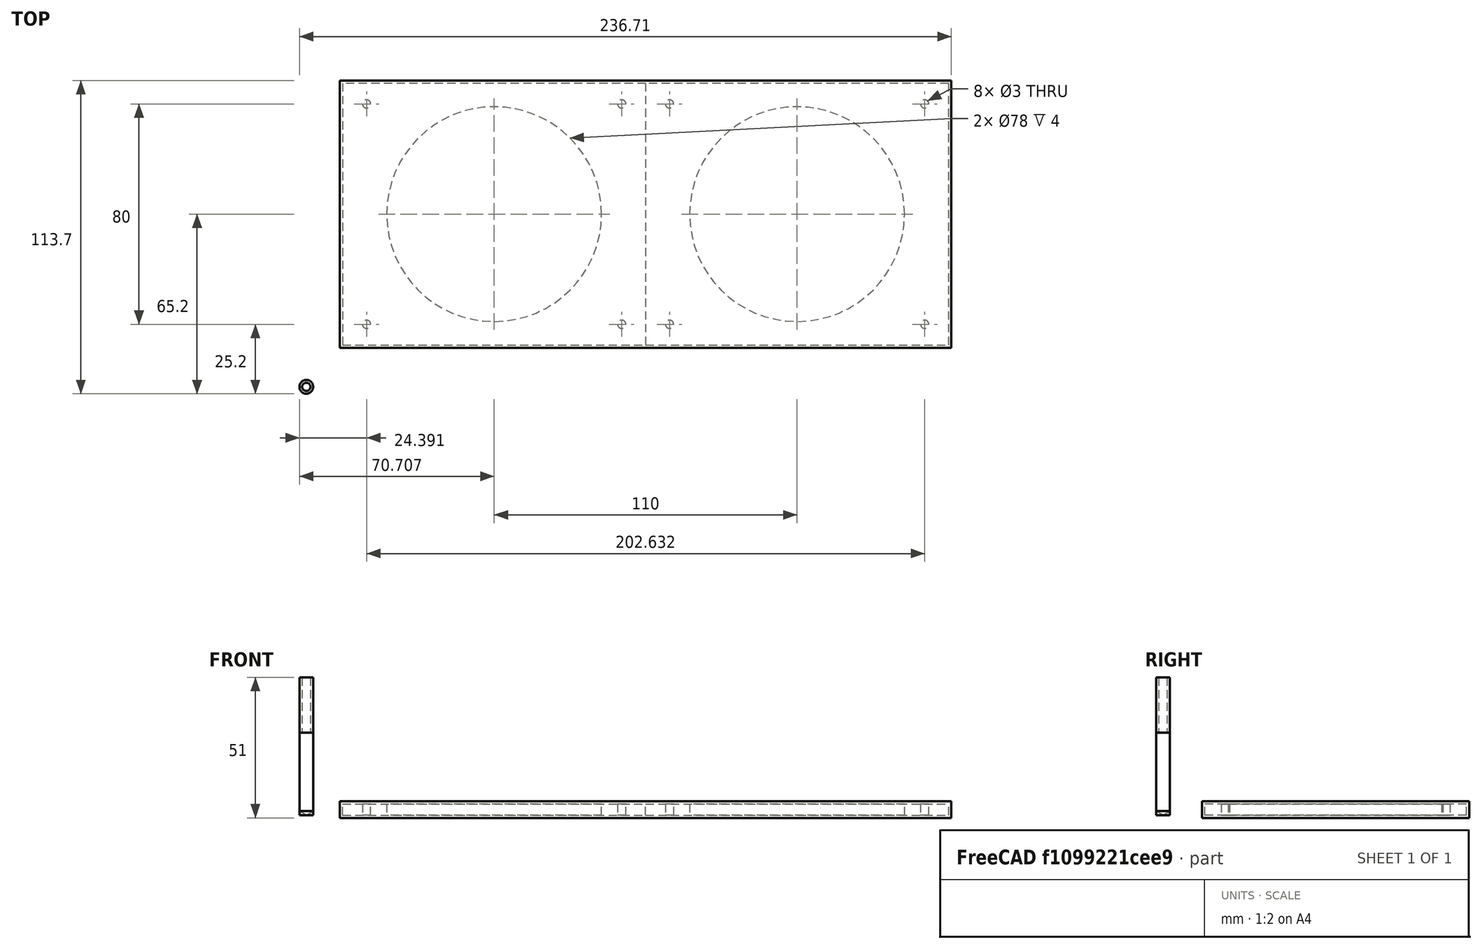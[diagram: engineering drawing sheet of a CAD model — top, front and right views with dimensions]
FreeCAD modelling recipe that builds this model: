
FCSTD DOCUMENT  (FreeCAD 1.0R39319 (Git))
Label: CAR_LASER_COMPONENTS_A4
License: All rights reserved
LicenseURL: https://en.wikipedia.org/wiki/All_rights_reserved
objects: Part::FeaturePython×10, App::FeaturePython×7, Path::FeaturePython×5, Sketcher::SketchObject×3, App::DocumentObjectGroup×3, PartDesign::Revolution×2, PartDesign::Body×2, Mesh::FeaturePython×1
note: 24 computed .brp shape members not serialized (recipe doc carries the construction recipe); baked Part::Feature solids carry a one-line shape summary decoded from their .brp

FEATURE [Sketcher::SketchObject] Sketch  label="A4"
  ArcFitTolerance = 0
  FullyConstrained = true
  MakeInternals = false
  sketch-geometry (12):
    g0: LineSegment [constr] StartX=0 StartY=0 StartZ=0 EndX=297 EndY=0 EndZ=0
    g1: LineSegment [constr] StartX=297 StartY=0 StartZ=0 EndX=297 EndY=420 EndZ=0
    g2: LineSegment [constr] StartX=297 StartY=420 StartZ=0 EndX=0 EndY=420 EndZ=0
    g3: LineSegment [constr] StartX=0 StartY=420 StartZ=0 EndX=0 EndY=0 EndZ=0
    g4: LineSegment StartX=0 StartY=0 StartZ=0 EndX=297 EndY=0 EndZ=0
    g5: LineSegment StartX=297 StartY=0 StartZ=0 EndX=297 EndY=420 EndZ=0
    g6: LineSegment StartX=297 StartY=420 StartZ=0 EndX=0 EndY=420 EndZ=0
    g7: LineSegment StartX=0 StartY=420 StartZ=0 EndX=0 EndY=0 EndZ=0
    g8: LineSegment [constr] StartX=0 StartY=420 StartZ=0 EndX=148.5 EndY=210 EndZ=0
    g9: LineSegment [constr] StartX=148.5 StartY=210 StartZ=0 EndX=297 EndY=0 EndZ=0
    g10: LineSegment StartX=148.5 StartY=210 StartZ=0 EndX=0 EndY=210 EndZ=0
    g11: LineSegment StartX=148.5 StartY=210 StartZ=0 EndX=297 EndY=210 EndZ=0
  constraints (30):
    c: Coincident(g0,g1)
    c: Coincident(g1,g2)
    c: Coincident(g2,g3)
    c: Coincident(g3,g0)
    c: Horizontal(g0)
    c: Horizontal(g2)
    c: Vertical(g1)
    c: Vertical(g3)
    c: Coincident(g0,g-1)
    c: DistanceY(g1,g1) = 420
    c: DistanceX(g2,g2) = 297
    c: Coincident(g4,g5)
    c: Coincident(g5,g6)
    c: Coincident(g6,g7)
    c: Coincident(g7,g4)
    c: Horizontal(g4)
    c: Horizontal(g6)
    c: Vertical(g5)
    c: Vertical(g7)
    c: Coincident(g4,g0)
    c: Coincident(g5,g1)
    c: Coincident(g8,g2)
    c: Coincident(g9,g0)
    c: Coincident(g9,g8)
    c: Equal(g9,g8)
    c: Coincident(g10,g8)
    c: Symmetric(g7,g7,g10)
    c: Horizontal(g10)
    c: Coincident(g11,g8)
    c: Symmetric(g5,g5,g11)
FEATURE [Part::FeaturePython] b_stearing_Flange_001_  label="stearing_Flange_001"  # a2plus imported part (geometry in sourceFile) (typed FeaturePython)
  Placement = pos=(-103.9,-12.3,0) rot=(0,0,1;0rad)
  a2p_Version = 0.4.68
  fixedPosition = true
  objectType = a2pPart
  sourceFile = ./stearing_Flange.FCStd
  subassemblyImport = false
  timeLastImport = 1.77512e+09
  updateColors = true
FEATURE [Part::FeaturePython] b_stearing_Flange_001_001  label="stearing_Flange_002"  # a2plus imported part (geometry in sourceFile) (typed FeaturePython)
  Placement = pos=(6.10001,-12.3,0) rot=(0,0,1;0rad)
  a2p_Version = 0.4.68
  fixedPosition = false
  objectType = a2pPart
  sourceFile = ./stearing_Flange.FCStd
  subassemblyImport = false
  timeLastImport = 1.77512e+09
  updateColors = true
FEATURE [App::FeaturePython] planeCoincident_001  label="planeCoincident_001__stearing_Flange_002"  # a2plus constraint (typed FeaturePython)
  Object1 = b_stearing_Flange_001_
  Object2 = b_stearing_Flange_001_001
  ParentTreeObject = -> b_stearing_Flange_001_
  SubElement1 = Face2
  SubElement2 = Face2
  Suppressed = false
  Type = plane
  directionConstraint = 0
  offset = 0
FEATURE [App::FeaturePython] planeCoincident_001_mirror  label="planeCoincident_001__stearing_Flange_001"  # a2plus constraint (typed FeaturePython)
  Object1 = b_stearing_Flange_001_
  Object2 = b_stearing_Flange_001_001
  ParentTreeObject = -> b_stearing_Flange_001_001
  SubElement1 = Face2
  SubElement2 = Face2
  Suppressed = false
  Type = plane
  directionConstraint = 0
  offset = 0
FEATURE [App::FeaturePython] planeCoincident_002  label="planeCoincident_002__stearing_Flange_002"  # a2plus constraint (typed FeaturePython)
  Object1 = b_stearing_Flange_001_
  Object2 = b_stearing_Flange_001_001
  ParentTreeObject = -> b_stearing_Flange_001_
  SubElement1 = Face3
  SubElement2 = Face1
  Suppressed = false
  Type = plane
  directionConstraint = 1
  offset = 0
FEATURE [App::FeaturePython] planeCoincident_002_mirror  label="planeCoincident_002__stearing_Flange_001"  # a2plus constraint (typed FeaturePython)
  Object1 = b_stearing_Flange_001_
  Object2 = b_stearing_Flange_001_001
  ParentTreeObject = -> b_stearing_Flange_001_001
  SubElement1 = Face3
  SubElement2 = Face1
  Suppressed = false
  Type = plane
  directionConstraint = 1
  offset = 0
FEATURE [App::FeaturePython] SetupSheet  # Path/CAM operation (typed FeaturePython)
  ClearanceHeightExpression = OpStockZMax+SetupSheet.ClearanceHeightOffset
  ClearanceHeightOffset = 5
  CoolantMode = 0
  CoolantModes = None | Flood | Mist
  FinalDepthExpression = OpFinalDepth
  HorizRapid = 0
  SafeHeightExpression = OpStockZMax+SetupSheet.SafeHeightOffset
  SafeHeightOffset = 3
  StartDepthExpression = OpStartDepth
  StepDownExpression = OpToolDiameter
  VertRapid = 0
FEATURE [Part::FeaturePython] Clone  label="Model-stearing_Flange_001"  # Draft clone (typed FeaturePython)
  AttacherType = Attacher::AttachEngine3D
  Fuse = false
  Objects = -> [b_stearing_Flange_001_]
  PathResource = Model
  Placement = pos=(-103.9,-12.3,0) rot=(0,0,1;0rad)
  Scale = (1,1,1)
FEATURE [Part::FeaturePython] Clone001  label="Model-stearing_Flange_002"  # Draft clone (typed FeaturePython)
  AttacherType = Attacher::AttachEngine3D
  Fuse = false
  Objects = -> [b_stearing_Flange_001_001]
  PathResource = Model
  Placement = pos=(6.10001,-12.3,0) rot=(0,0,1;0rad)
  Scale = (1,1,1)
FEATURE [App::DocumentObjectGroup] Model
  Group = -> [Clone,Clone001]
FEATURE [Part::FeaturePython] ToolBit  label="Endmill"  # Path/CAM toolbit (typed FeaturePython)
  BitPropertyNames = Chipload | CuttingEdgeHeight | Diameter | Flutes | Length | Material | ShankDiameter | SpindleDirection
  BitShape = <path>
  Chipload = 0
  CuttingEdgeHeight = 30
  Diameter = 5
  Flutes = 0
  Length = 50
  Material = 0
  ShankDiameter = 3
  ShapeName = endmill
  SpindleDirection = 0
FEATURE [Part::FeaturePython] Stock  # WARN: FeaturePython — macro-defined, semantics opaque (R4)
  Base = -> Model
  ExtXneg = 1
  ExtXpos = 1
  ExtYneg = 1
  ExtYpos = 1
  ExtZneg = 1
  ExtZpos = 1
  Placement = pos=(13.2071,15.2,0) rot=(0,0,1;0rad)
  StockType = FromBase
FEATURE [Mesh::FeaturePython] CutMaterial  # WARN: FeaturePython — macro-defined, semantics opaque (R4)
FEATURE [Part::FeaturePython] ToolBit001  label="Endmill003"  # Path/CAM toolbit (typed FeaturePython)
  BitPropertyNames = Chipload | CuttingEdgeHeight | Diameter | Flutes | Length | Material | ShankDiameter | SpindleDirection
  BitShape = <path>
  Chipload = 0
  CuttingEdgeHeight = 30
  Diameter = 5
  Flutes = 0
  Length = 50
  Material = 0
  ShankDiameter = 3
  ShapeName = endmill
  SpindleDirection = 0
FEATURE [Path::FeaturePython] TC__Default_Tool  label="TC: Default Tool"  # Path/CAM operation (typed FeaturePython)
  HorizFeed = 0
  HorizRapid = 0
  SpindleDir = 0
  SpindleSpeed = 0
  Tool = -> ToolBit001
  ToolNumber = 1
  VertFeed = 0
  VertRapid = 0
  expr: HorizRapid = SetupSheet.HorizRapid
  expr: VertRapid = SetupSheet.VertRapid
FEATURE [Path::FeaturePython] Engrave  # Path/CAM operation (typed FeaturePython)
  Active = true
  Base = -> [Clone]
  ClearanceHeight = 10
  CoolantMode = 0
  CycleTime = Cycletime Error
  FinalDepth = 0
  OpFinalDepth = 3.9
  OpStartDepth = 4
  OpStockZMax = 5
  OpStockZMin = -1
  OpToolDiameter = 5
  SafeHeight = 8
  StartDepth = 0
  StartVertex = 0
  StepDown = 0
  ToolController = -> TC__Default_Tool
  expr: ClearanceHeight = OpStockZMax + SetupSheet.ClearanceHeightOffset
  expr: FinalDepth = 0
  expr: SafeHeight = OpStockZMax + SetupSheet.SafeHeightOffset
  expr: StartDepth = 0
  expr: StepDown = 0
FEATURE [Path::FeaturePython] Engrave001  # Path/CAM operation (typed FeaturePython)
  Active = true
  Base = -> [Clone001]
  ClearanceHeight = 10
  CoolantMode = 0
  CycleTime = Cycletime Error
  FinalDepth = -1
  OpFinalDepth = -1
  OpStartDepth = 4
  OpStockZMax = 5
  OpStockZMin = -1
  OpToolDiameter = 5
  SafeHeight = 8
  StartDepth = 4
  StartVertex = 0
  StepDown = 5
  ToolController = -> TC__Default_Tool
  expr: ClearanceHeight = OpStockZMax + SetupSheet.ClearanceHeightOffset
  expr: FinalDepth = OpFinalDepth
  expr: SafeHeight = OpStockZMax + SetupSheet.SafeHeightOffset
  expr: StartDepth = OpStartDepth
  expr: StepDown = OpToolDiameter
FEATURE [App::DocumentObjectGroup] Operations
  Group = -> [Engrave,Engrave001]
FEATURE [Sketcher::SketchObject] Sketch001
  ArcFitTolerance = 0
  AttachmentSupport = -> [XZ_Plane]
  FullyConstrained = true
  MakeInternals = false
  MapMode = 5
  Placement = pos=(0,0,0) rot=(1,0,0;1.5708rad)
  expr: Constraints[10] = <<Attributes>>.Length
  expr: Constraints[16] = <<Attributes>>.ShankDiameter
  expr: Constraints[18] = <<Attributes>>.CuttingEdgeHeight
  expr: Constraints[9] = <<Attributes>>.Diameter
  sketch-geometry (8):
    g0: LineSegment StartX=0 StartY=50 StartZ=0 EndX=0 EndY=0 EndZ=0
    g1: LineSegment StartX=0 StartY=0 StartZ=0 EndX=2.5 EndY=0 EndZ=0
    g2: LineSegment StartX=2.5 StartY=0 StartZ=0 EndX=2.5 EndY=30 EndZ=0
    g3: LineSegment StartX=1.5 StartY=50 StartZ=0 EndX=0 EndY=50 EndZ=0
    g4: LineSegment [constr] StartX=2.5 StartY=0 StartZ=0 EndX=-2.5 EndY=0 EndZ=0
    g5: LineSegment StartX=1.5 StartY=29.99 StartZ=0 EndX=2.5 EndY=30 EndZ=0
    g6: LineSegment StartX=1.5 StartY=50 StartZ=0 EndX=1.5 EndY=29.99 EndZ=0
    g7: LineSegment [constr] StartX=-1.5 StartY=50 StartZ=0 EndX=1.5 EndY=50 EndZ=0
  constraints (21):
    c: Vertical(g0)
    c: Coincident(g0,g1)
    c: Horizontal(g1)
    c: Coincident(g1,g2)
    c: Vertical(g2)
    c: Horizontal(g3)
    c: Coincident(g0,g3)
    c: Coincident(g4,g1)
    c: Symmetric(g1,g4,g0)
    c: DistanceX(g4,g4) = 5
    c: DistanceY(g2,g3) = 50
    c: Coincident(g2,g5)
    c: Vertical(g6)
    c: Coincident(g3,g6)
    c: Symmetric(g7,g7,g0)
    c: Coincident(g7,g3)
    c: DistanceX(g7,g7) = 3
    c: Coincident(g5,g6)
    c: DistanceY(g2) = 30
    c: Coincident(g0,g-1)
    c: DistanceY(g5,g2) = 0.01
FEATURE [PartDesign::Revolution] Revolution
  AllowMultiFace = false
  Angle = 360
  Angle2 = 60
  Axis = (0,2e-16,1)
  Base = (0,0,0)
  Placement = pos=(0,0,0) rot=(1,0,0;1.5708rad)
  Profile = -> Sketch001
  ReferenceAxis = -> Sketch001 [V_Axis]
  Reversed = true
  Suppressed = false
  Type = 0
FEATURE [App::FeaturePython] PropertyBag  label="Attributes"  # WARN: FeaturePython — macro-defined, semantics opaque (R4)
  Chipload = 0
  CustomPropertyGroups = Attributes | Shape
  CuttingEdgeHeight = 30
  Diameter = 5
  Flutes = 0
  Length = 50
  Material = 0
  ShankDiameter = 3
  SpindleDirection = 0
FEATURE [PartDesign::Body] Body  label="Endmill005"
  AllowCompound = false
  Group = -> [Sketch001,Revolution,PropertyBag]
  Origin = -> Origin
  Tip = -> Revolution
FEATURE [Part::FeaturePython] ToolBit002  label="Endmill006"  # Path/CAM toolbit (typed FeaturePython)
  BitBody = -> Body
  BitPropertyNames = Chipload | CuttingEdgeHeight | Diameter | Flutes | Length | Material | ShankDiameter | SpindleDirection
  BitShape = <path>
  Chipload = 0
  CuttingEdgeHeight = 30
  Diameter = 5
  Flutes = 0
  Length = 50
  Material = 0
  ShankDiameter = 3
  ShapeName = endmill
  SpindleDirection = 0
FEATURE [Part::FeaturePython] ToolBit003  label="5mm Drill"  # Path/CAM toolbit (typed FeaturePython)
  BitPropertyNames = Chipload | Diameter | Flutes | Length | Material | TipAngle
  BitShape = <path>
  Chipload = 0
  Diameter = 5
  File = <path>
  Flutes = 0
  Length = 50
  Material = 0
  ShapeName = drill
  TipAngle = 119
FEATURE [Sketcher::SketchObject] Sketch002
  ArcFitTolerance = 0
  AttachmentSupport = -> [XZ_Plane001]
  FullyConstrained = true
  MakeInternals = false
  MapMode = 5
  Placement = pos=(0,0,0) rot=(1,0,0;1.5708rad)
  expr: Constraints[13] = <<Attributes001>>.TipAngle
  expr: Constraints[14] = <<Attributes001>>.Diameter
  expr: Constraints[15] = <<Attributes001>>.Length
  sketch-geometry (7):
    g0: LineSegment StartX=0 StartY=50 StartZ=0 EndX=0 EndY=0 EndZ=0
    g1: LineSegment StartX=0 StartY=2e-16 StartZ=0 EndX=2.5 EndY=1.47261 EndZ=0
    g2: LineSegment StartX=2.5 StartY=1.47261 StartZ=0 EndX=2.5 EndY=50 EndZ=0
    g3: LineSegment StartX=2.5 StartY=50 StartZ=0 EndX=0 EndY=50 EndZ=0
    g4: LineSegment [constr] StartX=2.5 StartY=1.47261 StartZ=0 EndX=-2.5 EndY=1.47261 EndZ=0
    g5: LineSegment [constr] StartX=-2.5 StartY=1.47261 StartZ=0 EndX=0 EndY=0 EndZ=0
    g6: LineSegment [constr] StartX=0 StartY=2e-16 StartZ=0 EndX=2.5 EndY=1.47261 EndZ=0
  constraints (17):
    c: Vertical(g0)
    c: Coincident(g0,g1)
    c: Coincident(g1,g2)
    c: Vertical(g2)
    c: Coincident(g2,g3)
    c: Horizontal(g3)
    c: Coincident(g0,g3)
    c: Coincident(g4,g5)
    c: Coincident(g5,g6)
    c: Coincident(g6,g4)
    c: Coincident(g1,g4)
    c: Coincident(g5,g0)
    c: Symmetric(g4,g1,g0)
    c: Angle(g1,g5) = 2.07694
    c: DistanceX(g4,g4) = 5
    c: DistanceY(g0,g0) = 50
    c: Coincident(g0,g-1)
FEATURE [PartDesign::Revolution] Revolution001
  AllowMultiFace = false
  Angle = 360
  Angle2 = 60
  Axis = (0,2e-16,1)
  Base = (0,0,0)
  Placement = pos=(0,0,0) rot=(1,0,0;1.5708rad)
  Profile = -> Sketch002
  ReferenceAxis = -> Sketch002 [V_Axis]
  Reversed = true
  Suppressed = false
  Type = 0
FEATURE [App::FeaturePython] PropertyBag001  label="Attributes001"  # WARN: FeaturePython — macro-defined, semantics opaque (R4)
  Chipload = 0
  CustomPropertyGroups = Attributes | Shape
  Diameter = 5
  Flutes = 0
  Length = 50
  Material = 0
  TipAngle = 119
FEATURE [PartDesign::Body] Body001  label="Drill001"
  AllowCompound = false
  Group = -> [Sketch002,Revolution001,PropertyBag001]
  Origin = -> Origin001
  Tip = -> Revolution001
FEATURE [Part::FeaturePython] ToolBit004  label="5mm Drill002"  # Path/CAM toolbit (typed FeaturePython)
  BitBody = -> Body001
  BitPropertyNames = Chipload | Diameter | Flutes | Length | Material | TipAngle
  BitShape = <path>
  Chipload = 0
  Diameter = 5
  Flutes = 0
  Length = 50
  Material = 0
  ShapeName = drill
  TipAngle = 119
FEATURE [Path::FeaturePython] _mm_Drill  label="5mm Drill001"  # Path/CAM operation (typed FeaturePython)
  HorizFeed = 0
  HorizRapid = 0
  SpindleDir = 0
  SpindleSpeed = 0
  Tool = -> ToolBit003
  ToolNumber = 2
  VertFeed = 0
  VertRapid = 0
  expr: HorizRapid = SetupSheet.HorizRapid
  expr: VertRapid = SetupSheet.VertRapid
FEATURE [App::DocumentObjectGroup] Tools
  Group = -> [TC__Default_Tool,_mm_Drill]
FEATURE [Path::FeaturePython] Job  # Path/CAM operation (typed FeaturePython)
  CycleTime = 00:00:00
  Fixtures = G54
  GeometryTolerance = 0.01
  JobType = 0
  Model = -> Model
  Operations = -> Operations
  OrderOutputBy = 0
  PostProcessor = 1
  PostProcessorOutputFile = <userpath>/Documents/papyrusplane/NC_CAR2/NC_CAR_STEARING_RAW.nc
  SetupSheet = -> SetupSheet
  SplitOutput = false
  Stock = -> Stock
  Tools = -> Tools
note: 6 file-system paths scrubbed to <path> (originals preserved in the JSON sidecar)
